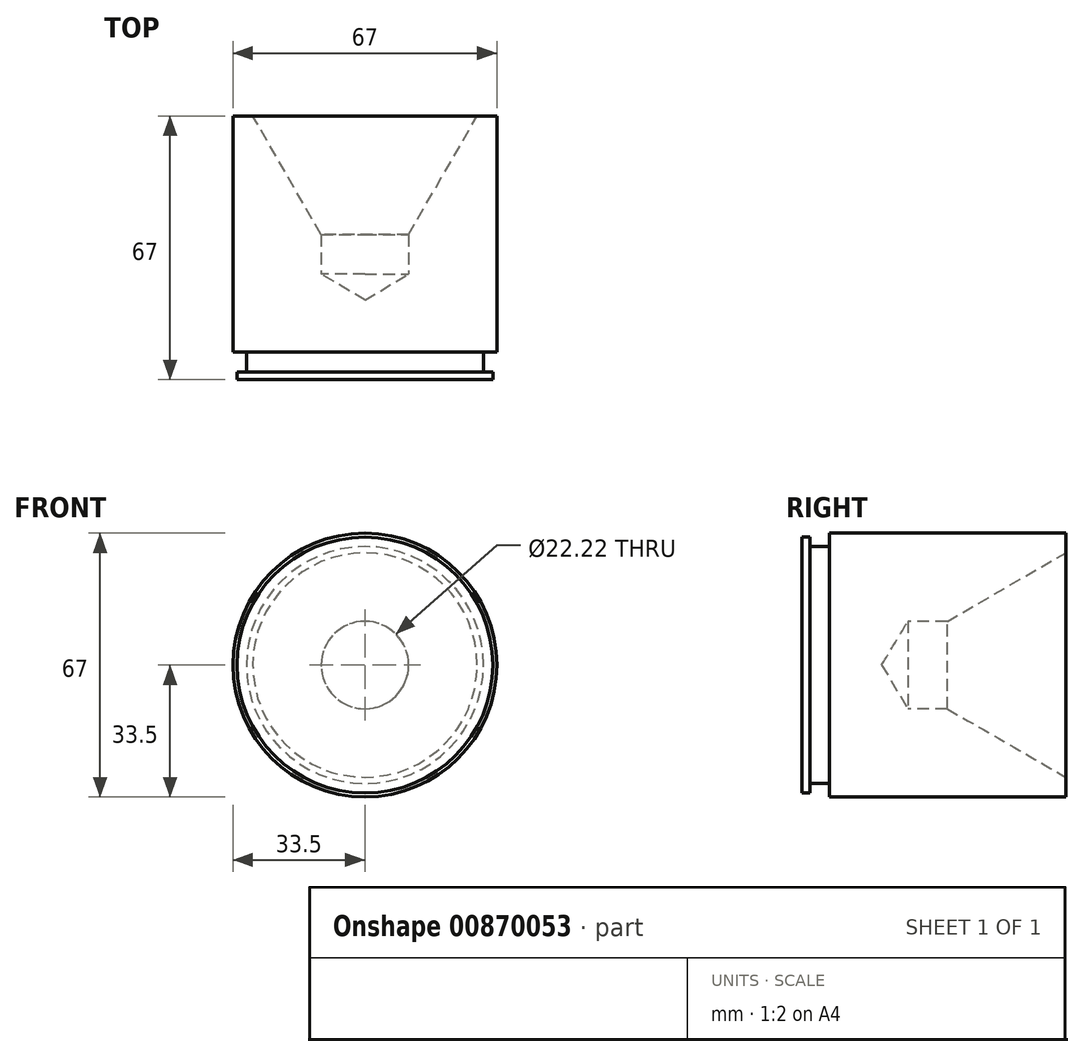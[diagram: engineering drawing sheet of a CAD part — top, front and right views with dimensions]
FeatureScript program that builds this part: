
annotation { "Feature Type Name" : "Feature", "Feature Type Description" : "" }
export const myFeature = defineFeature(function(context is Context, id is Id, definition is map)
    precondition{}
    {
        {
            var Q0;
            Q0=qCreatedBy(makeId("Right.planeOp"),FACE);
            var sketch = newSketch(context, id + "F0", { "sketchPlane" : qUnion([Q0])});
            skLineSegment(sketch, "E0", {"start": v(0, 0) * mm, "end": v(0, 32.5) * mm});
            skLineSegment(sketch, "E1", {"start": v(0, 32.5) * mm, "end": v(2, 32.5) * mm});
            skLineSegment(sketch, "E2", {"start": v(2, 32.5) * mm, "end": v(2, 30.1) * mm});
            skLineSegment(sketch, "E3", {"start": v(2, 30.1) * mm, "end": v(7, 30.1) * mm});
            skLineSegment(sketch, "E4", {"start": v(7, 30.1) * mm, "end": v(7, 33.5) * mm});
            skLineSegment(sketch, "E5", {"start": v(7, 33.5) * mm, "end": v(67, 33.5) * mm});
            skLineSegment(sketch, "E6", {"start": v(67, 33.5) * mm, "end": v(67, 28.5) * mm});
            skLineSegment(sketch, "E7", {"start": v(36.88, 11.1) * mm, "end": v(26.68, 11.1) * mm});
            skLineSegment(sketch, "E8", {"start": v(26.68, 11.1) * mm, "end": v(20, 0) * mm});
            skLineSegment(sketch, "E9", {"start": v(20, 0) * mm, "end": v(0, 0) * mm});
            skLineSegment(sketch, "E10", {"start": v(67, 28.5) * mm, "end": v(36.88, 11.11) * mm});
            skLineSegment(sketch, "E11", {"start": v(0, 0) * mm, "end": v(184.82, 0) * mm, "construction": true});
            skSolve(sketch);
        }
        {
            var Q0;
            Q0=makeQuery(id+"F0.imprint","IMPRINT",FACE,{"disambiguationData":[TD([[makeQuery(id+"F0.imprint","IMPRINT",EDGE,{"derivedFrom":sQuery(id+"F0.wireOp",EDGE,"E0")}),-1.0]])]});
            var sketch = newSketch(context, id + "F1", { "sketchPlane" : qUnion([Q0])});
            skLineSegment(sketch, "E12", {"start": v(0, 0) * mm, "end": v(0, 35) * mm});
            skLineSegment(sketch, "E13", {"start": v(0, 35) * mm, "end": v(67, 35) * mm});
            skLineSegment(sketch, "E14", {"start": v(67, 35) * mm, "end": v(67, 28.5) * mm});
            skLineSegment(sketch, "E15", {"start": v(67, 28.5) * mm, "end": v(36.88, 11.1) * mm});
            skLineSegment(sketch, "E16", {"start": v(36.88, 11.1) * mm, "end": v(26.88, 11.1) * mm});
            skLineSegment(sketch, "E17", {"start": v(26.88, 11.1) * mm, "end": v(20.2, 0) * mm});
            skLineSegment(sketch, "E18", {"start": v(20.2, 0) * mm, "end": v(0, 0) * mm});
            skLineSegment(sketch, "E19", {"start": v(0, 0) * mm, "end": v(70.6, 0) * mm, "construction": true});
            skSolve(sketch);
        }
        {
            var Q0;
            Q0 = qSketchRegion(id + "F1", true);
            var Q1;
            Q1=sQuery(id+"F1.wireOp",EDGE,"E19");
            revolve(context, id + "F2", {"surfaceOperationType" : NewSurfaceOperationType.NEW, "entities" : qUnion([Q0]), "axis" : qUnion([Q1]), "revolveType" : RevolveType.FULL});
        }
        {
            var Q0;
            Q0=qCreatedBy(makeId("Right.planeOp"),FACE);
            var sketch = newSketch(context, id + "F3", { "sketchPlane" : qUnion([Q0])});
            skLineSegment(sketch, "E20", {"start": v(68.53, 33.5) * mm, "end": v(7, 33.5) * mm});
            skLineSegment(sketch, "E21", {"start": v(7, 33.5) * mm, "end": v(7, 30.1) * mm});
            skLineSegment(sketch, "E22", {"start": v(7, 30.1) * mm, "end": v(2, 30.1) * mm});
            skLineSegment(sketch, "E23", {"start": v(2, 30.1) * mm, "end": v(2, 32.5) * mm});
            skLineSegment(sketch, "E24", {"start": v(2, 32.5) * mm, "end": v(0, 32.5) * mm});
            skLineSegment(sketch, "E25", {"start": v(0, 32.5) * mm, "end": v(0, 44.95) * mm});
            skLineSegment(sketch, "E26", {"start": v(0, 44.95) * mm, "end": v(69.65, 44.95) * mm});
            skLineSegment(sketch, "E27", {"start": v(69.65, 44.95) * mm, "end": v(68.53, 33.5) * mm});
            skLineSegment(sketch, "E28", {"start": v(0, 0) * mm, "end": v(112.8, 0) * mm, "construction": true});
            skSolve(sketch);
        }
        {
            var Q0;
            Q0 = qSketchRegion(id + "F3", true);
            var Q1;
            Q1=sQuery(id+"F3.wireOp",EDGE,"E28");
            revolve(context, id + "F4", {"operationType" : NewBodyOperationType.REMOVE, "surfaceOperationType" : NewSurfaceOperationType.NEW, "entities" : qUnion([Q0]), "axis" : qUnion([Q1]), "revolveType" : RevolveType.FULL, "oppositeDirection" : true});
        }
    });
